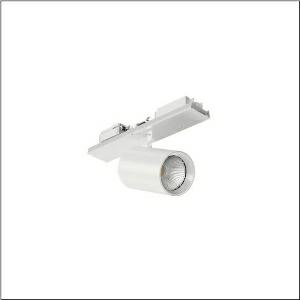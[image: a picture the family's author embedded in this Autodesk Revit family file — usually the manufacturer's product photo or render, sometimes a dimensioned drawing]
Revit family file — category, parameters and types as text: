
# Revit family: licross_r__spot_31_51sl147a43b_2678
name_source: partatom
category: Lighting Fixtures
units: mm (PartAtom-declared; Revit-internal decimal feet)

## family parameters
Cut with Voids When Loaded = No
Host = Face
Light Source = No
Part Type = Normal
Room Calculation Point = No
Round Connector Dimension = Use Diameter
Shared = No

## types (1)
- --- (1 x LED, 3720 lm, 27.9 W, 4000K)
    Apparent Load = 28 VA
    CIE Flux Codes = 93 97 100 100 100
    Color Rendering = 90
    Color Temperature = 4000K
    Default Elevation = 1800 mm
    Description = Licross® Spot 31, directional spotlight, light control with lens, of plastic, LED rated luminous flux: 3.720lm, light colour: 940, with plug, 3-pole, with phase selection, mains connection: 220..240V, AC, 50/60Hz, of aluminium, traffic white (RAL 9016), length: 300mm, diameter: 90mm, protection rating (complete): IP20, insulation class (complete): insulation class I (protective earthing), certification: CE, packaging unit: 1 piece
    Height = 175 mm
    Lamp = 1 x LED
    Lamp Light Flux = 3720 lm
    Lamp Power = 27.9 W
    Lamp count = 1
    Length = 90 mm
    Luminous efficacy = 133 lm/W
    Manufacturer = Siteco
    ModVariant = No
    Model = 51SL147A43B
    Mounting Place = Ceiling
    Mounting Type = Pendant
    Number of Poles = 1
    OnlyDefault = Yes
    Power Factor = 1
    Product Name = Licross® Spot 31
    Product group = directional spotlight
    ProductGroupID = 906
    Protection Class = Protection class I
    Protection Degree = IP 20
    RLX_Detail_Level = 1
    RLX_Emergency_Light_Flux = 0 lm
    RLX_Emergency_Type = 0
    RLX_Emergency_Type_DB = No
    RlxData = <blob elided: 14849 chars, md5=befc3ca3>
    Socket = socket
    Standby Power = 0 W
    System Light Flux = 3720 lm
    System Power = 28 W
    Type Comments = factory setting: luminous flux: 100 % | (ON | ON | ON) | 700 mA
    Type Image = l_1245720.jpg
    URL = http://relux.com
    VarID = @adj_132040
    Voltage = 0 V
    Weight = 0.00 kg
    Width = 0 mm  [stored 0 ft]

note: [stored X ft] marks values corroborated as IEEE doubles in the binary element streams (Revit-internal decimal feet)

## geometry (parser evidence)
native form markers: Sweep x12
no freeform markers — native parametric forms only
